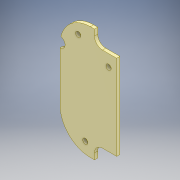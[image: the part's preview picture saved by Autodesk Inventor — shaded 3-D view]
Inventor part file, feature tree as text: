
AUTODESK INVENTOR PART (.ipt)
format: ipt  version: 2019 (Build 230136000, 136)  size: 155,648 bytes
history: native  units: mm
features: extrude x4, sketch x4, fillet x1
ambient origin geometry x8: Origin, YZ Plane, XZ Plane, XY Plane, X Axis, Y Axis, Z Axis, Center Point
bodies: Solide1 (feature_tree)
feature tree (9):
  extrude  "Extrusion1"  Depth=28.0mm
  fillet  "Congé1"  Radius=56.0mm
  extrude  "Extrusion3"  Depth=28.0mm
  extrude  "Extrusion4"  Depth=14.0mm
  extrude  "Extrusion5"  Depth=1.6mm TaperAngle=0.0deg
  sketch  "Esquisse1"
  sketch  "Esquisse2"
  sketch  "Esquisse3"
  sketch  "Esquisse4"
